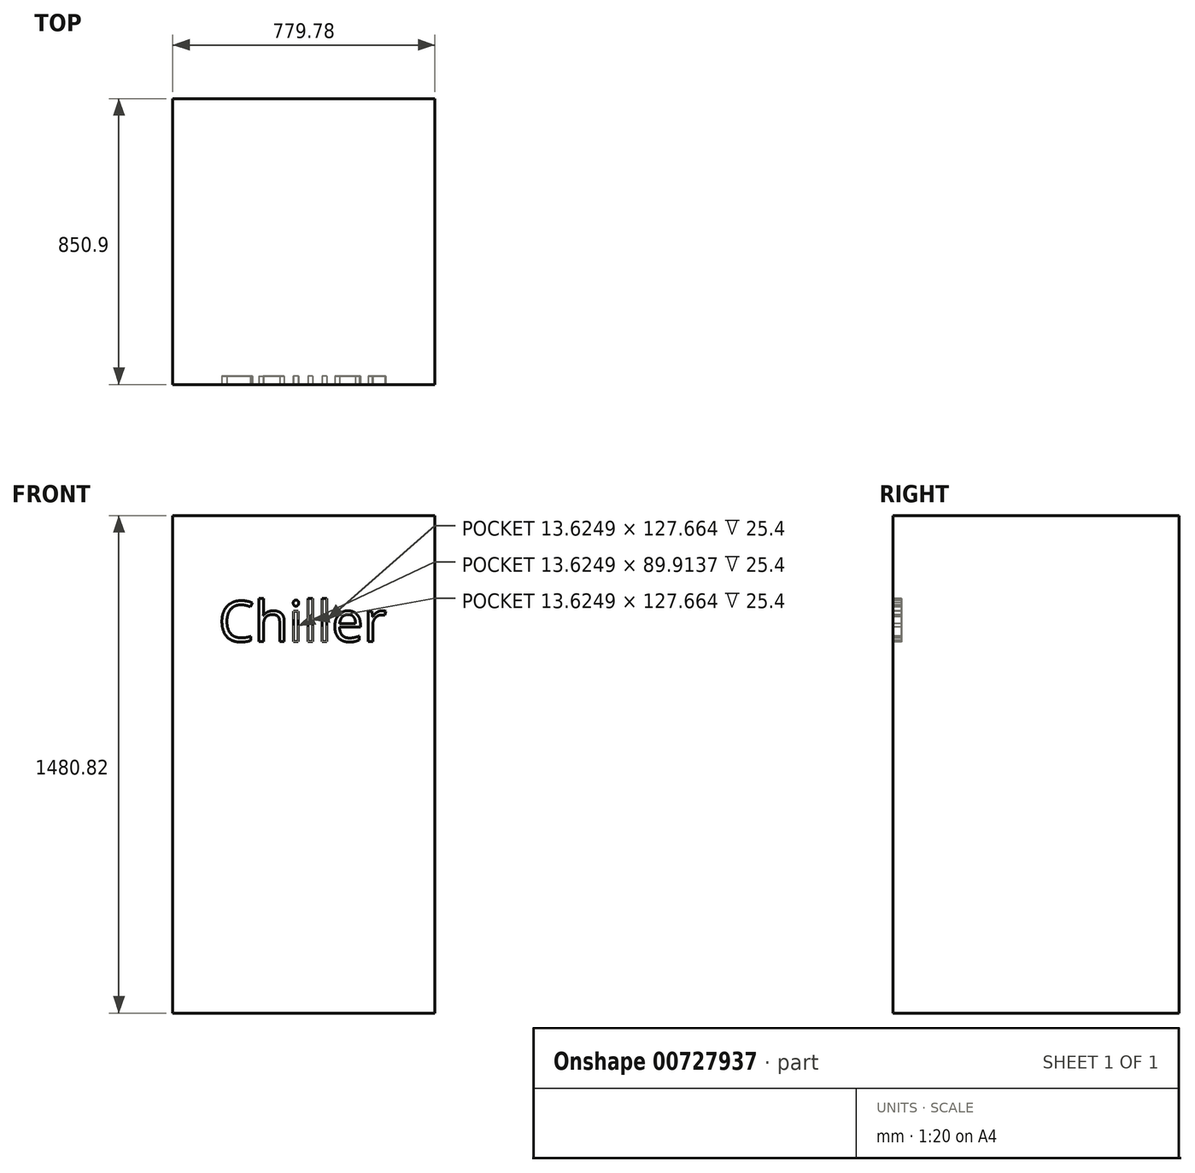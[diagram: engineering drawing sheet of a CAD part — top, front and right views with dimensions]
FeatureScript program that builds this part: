
annotation { "Feature Type Name" : "Feature", "Feature Type Description" : "" }
export const myFeature = defineFeature(function(context is Context, id is Id, definition is map)
    precondition{}
    {
        {
            var Q0;
            Q0=qCreatedBy(makeId("Top.planeOp"),FACE);
            var sketch = newSketch(context, id + "F0", { "sketchPlane" : qUnion([Q0])});
            skLineSegment(sketch, "E0.bottom", {"start": v(389.9, -425.45) * mm, "end": v(-389.9, -425.45) * mm});
            skLineSegment(sketch, "E0.top", {"start": v(389.9, 425.45) * mm, "end": v(-389.9, 425.45) * mm});
            skLineSegment(sketch, "E0.left", {"start": v(389.9, -425.45) * mm, "end": v(389.9, 425.45) * mm});
            skLineSegment(sketch, "E0.right", {"start": v(-389.9, -425.45) * mm, "end": v(-389.9, 425.45) * mm});
            skPoint(sketch, "E0.middle", {"position": v(0, 0) * mm});
            skSolve(sketch);
        }
        {
            var Q0;
            Q0 = qSketchRegion(id + "F0", true);
            extrude(context, id + "F1", {"entities" : qUnion([Q0]), "depth" : 1480.82 * mm, "offsetDistance" : 25.4 * mm});
        }
        {
            var Q0;
            Q0=makeQuery(id+"F1.opExtrude","SWEPT_FACE",FACE,{"disambiguationData":[OSD([sQuery(id+"F0.wireOp",EDGE,"E0.bottom")])]});
            var sketch = newSketch(context, id + "F2", { "sketchPlane" : qUnion([Q0])});
            skText(sketch, "E1", { "text": "Chiller", "fontName": "OpenSans-Regular.ttf"});
            const initialGuessF2  = {"E1": [-0.254, 1.10585, 1, 0, 0.12097]};
            skSetInitialGuess(sketch, initialGuessF2);
            skSolve(sketch);
        }
        {
            var Q0;
            Q0 = qSketchRegion(id + "F2", true);
            extrude(context, id + "F3", {"entities" : qUnion([Q0]), "operationType" : NewBodyOperationType.REMOVE, "oppositeDirection" : true, "depth" : 25.4 * mm, "offsetDistance" : 25.4 * mm});
        }
    });
